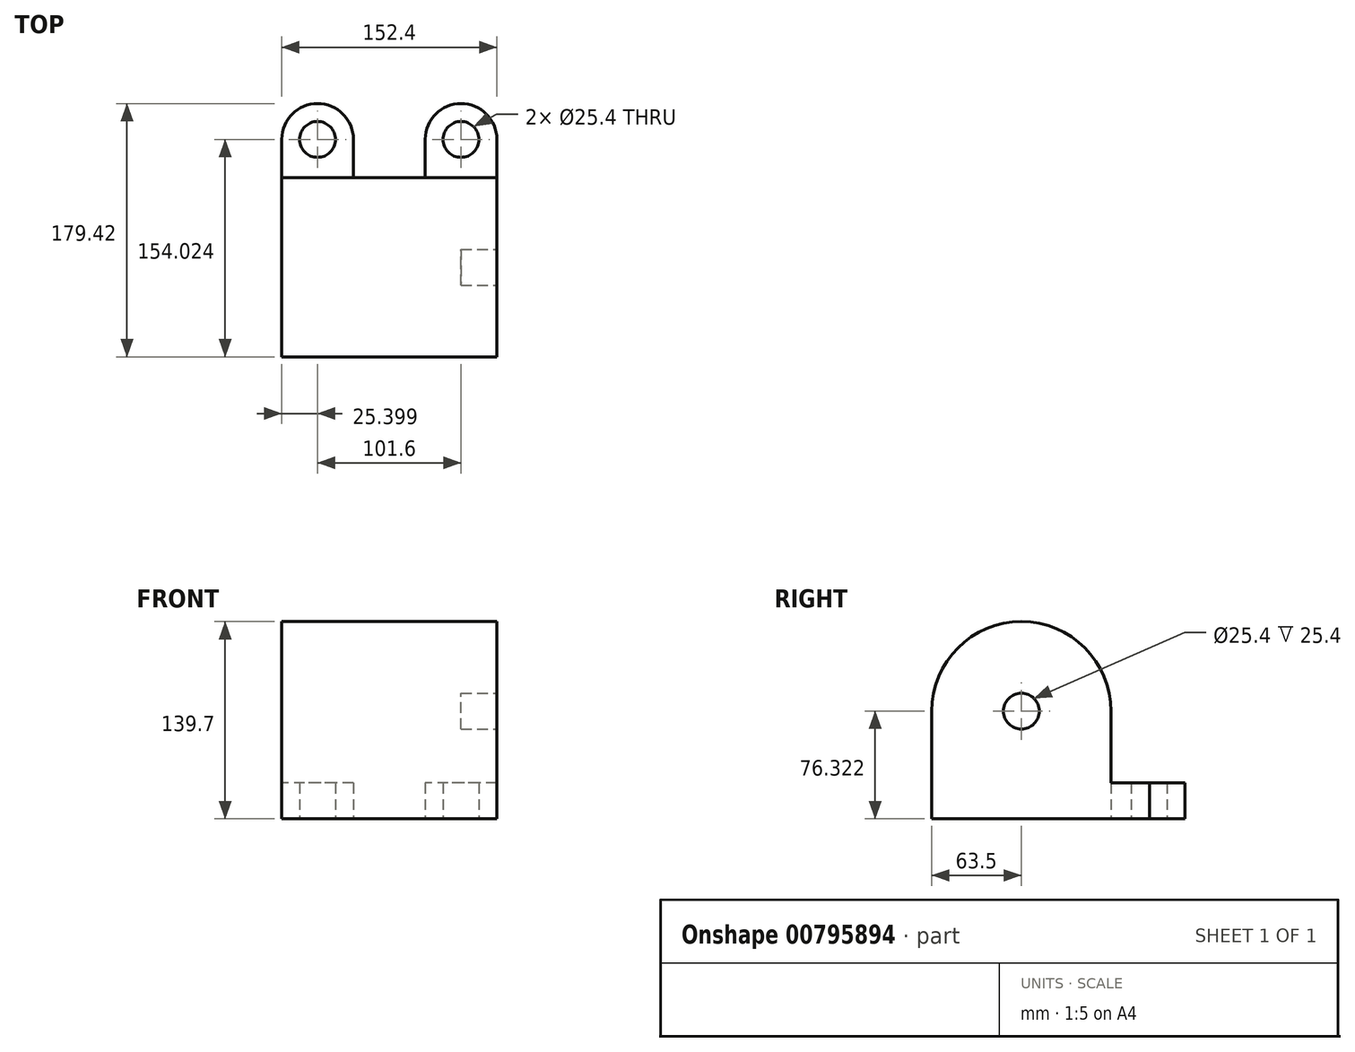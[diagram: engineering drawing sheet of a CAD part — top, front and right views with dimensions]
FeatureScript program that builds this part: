
annotation { "Feature Type Name" : "Feature", "Feature Type Description" : "" }
export const myFeature = defineFeature(function(context is Context, id is Id, definition is map)
    precondition{}
    {
        {
            var Q0;
            Q0=qCreatedBy(makeId("Right.planeOp"),FACE);
            var sketch = newSketch(context, id + "F0", { "sketchPlane" : qUnion([Q0])});
            skArc(sketch, "E0", {"start": v(63.5, 76.2) * mm, "mid": v(0, 139.7) * mm, "end": v(-63.5, 76.2) * mm});
            skLineSegment(sketch, "E1", {"start": v(63.5, 76.2) * mm, "end": v(63.5, 0) * mm});
            skLineSegment(sketch, "E2", {"start": v(-63.5, 76.2) * mm, "end": v(-63.5, 0) * mm});
            skLineSegment(sketch, "E3", {"start": v(-63.5, 0) * mm, "end": v(63.5, 0) * mm});
            skLineSegment(sketch, "E4.left", {"start": v(63.5, 0) * mm, "end": v(63.5, 12.7) * mm});
            skLineSegment(sketch, "E5.left", {"start": v(-63.5, 0) * mm, "end": v(-63.5, 12.7) * mm});
            skSolve(sketch);
        }
        {
            var Q0;
            Q0 = qSketchRegion(id + "F0", true);
            extrude(context, id + "F1", {"entities" : qUnion([Q0]), "oppositeDirection" : true, "depth" : 152.4 * mm, "offsetDistance" : 25.4 * mm});
        }
        {
            var Q0;
            Q0=makeQuery(id+"F1.opExtrude","CAP_FACE",FACE,{"disambiguationData":[OSD([sQuery(id+"F0.wireOp",EDGE,"E0"),sQuery(id+"F0.wireOp",EDGE,"E1"),sQuery(id+"F0.wireOp",EDGE,"E2"),sQuery(id+"F0.wireOp",EDGE,"E3"),sQuery(id+"F0.wireOp",EDGE,"E4.bottom"),sQuery(id+"F0.wireOp",EDGE,"E4.top"),sQuery(id+"F0.wireOp",EDGE,"E4.right"),sQuery(id+"F0.wireOp",EDGE,"E5.bottom"),sQuery(id+"F0.wireOp",EDGE,"E5.top"),sQuery(id+"F0.wireOp",EDGE,"E5.right")])],"isStart":true});
            var sketch = newSketch(context, id + "F2", { "sketchPlane" : qUnion([Q0])});
            skSolve(sketch);
        }
        {
            var Q0;
            Q0=qCreatedBy(makeId("Top.planeOp"),FACE);
            var sketch = newSketch(context, id + "F3", { "sketchPlane" : qUnion([Q0])});
            skCircle(sketch, "E6", {"center": v(-25.4, 90.52) * mm, "radius": 12.7 * mm});
            skArc(sketch, "E7", {"start": v(0, 90.79) * mm, "mid": v(-25.4, 115.92) * mm, "end": v(-50.8, 90.79) * mm});
            skLineSegment(sketch, "E8.bottom", {"start": v(0, 63.5) * mm, "end": v(-50.8, 63.5) * mm});
            skLineSegment(sketch, "E8.top", {"start": v(0, 90.79) * mm, "end": v(0, 90.79) * mm});
            skLineSegment(sketch, "E8.left", {"start": v(0, 63.5) * mm, "end": v(0, 90.79) * mm});
            skLineSegment(sketch, "E8.right", {"start": v(-50.8, 63.5) * mm, "end": v(-50.8, 90.79) * mm});
            skCircle(sketch, "E9", {"center": v(-127, 90.52) * mm, "radius": 12.7 * mm});
            skArc(sketch, "E10", {"start": v(-101.6, 90.79) * mm, "mid": v(-127, 115.92) * mm, "end": v(-152.4, 90.79) * mm});
            skLineSegment(sketch, "E11.bottom", {"start": v(-101.6, 63.5) * mm, "end": v(-152.4, 63.5) * mm});
            skLineSegment(sketch, "E11.top", {"start": v(-101.6, 90.79) * mm, "end": v(-101.6, 90.79) * mm});
            skLineSegment(sketch, "E11.left", {"start": v(-101.6, 63.5) * mm, "end": v(-101.6, 90.79) * mm});
            skLineSegment(sketch, "E11.right", {"start": v(-152.4, 63.5) * mm, "end": v(-152.4, 90.79) * mm});
            skSolve(sketch);
        }
        {
            var Q0;
            Q0=makeQuery(id+"F3.imprint","IMPRINT",FACE,{"disambiguationData":[TD([[makeQuery(id+"F3.imprint","IMPRINT",EDGE,{"derivedFrom":sQuery(id+"F3.wireOp",EDGE,"E6")}),-1.0]])]});
            var Q1;
            Q1=makeQuery(id+"F3.imprint","IMPRINT",FACE,{"disambiguationData":[TD([[makeQuery(id+"F3.imprint","IMPRINT",EDGE,{"derivedFrom":sQuery(id+"F3.wireOp",EDGE,"E9")}),-1.0]])]});
            extrude(context, id + "F4", {"entities" : qUnion([Q0, Q1]), "operationType" : NewBodyOperationType.ADD, "depth" : 25.4 * mm, "offsetDistance" : 25.4 * mm});
        }
        {
            var Q0;
            Q0=makeQuery(id+"F2.imprint","IMPRINT",FACE,{"disambiguationData":[TD([[makeQuery(id+"F2.imprint","IMPRINT",EDGE,{"derivedFrom":makeQuery(id+"F1.opExtrude","CAP_EDGE",EDGE,{"disambiguationData":[OSD([sQuery(id+"F0.wireOp",EDGE,"E0")])],"isStart":true})}),1.0]])]});
            var sketch = newSketch(context, id + "F5", { "sketchPlane" : qUnion([Q0])});
            skCircle(sketch, "E12", {"center": v(0, 76.32) * mm, "radius": 12.7 * mm});
            skSolve(sketch);
        }
        {
            var Q0;
            Q0 = qSketchRegion(id + "F5", true);
            extrude(context, id + "F6", {"entities" : qUnion([Q0]), "operationType" : NewBodyOperationType.REMOVE, "oppositeDirection" : true, "depth" : 25.4 * mm, "offsetDistance" : 25.4 * mm});
        }
    });
